FCSTD DOCUMENT  (FreeCAD 0.19R0.19.2)
Label: enclosure_000
License: All rights reserved
LicenseURL: http://en.wikipedia.org/wiki/All_rights_reserved
objects: Sketcher::SketchObject×1
note: 1 computed .brp shape members not serialized (recipe doc carries the construction recipe); baked Part::Feature solids carry a one-line shape summary decoded from their .brp

FEATURE [Sketcher::SketchObject] Sketch
  FullyConstrained = true
  sketch-geometry (13):
    g0: LineSegment StartX=0 StartY=0 StartZ=0 EndX=98 EndY=0 EndZ=0
    g1: LineSegment StartX=117 StartY=19 StartZ=0 EndX=117 EndY=38 EndZ=0
    g2: ArcOfCircle CenterX=98 CenterY=19 CenterZ=0 NormalX=0 NormalY=0 NormalZ=1 AngleXU=0 Radius=19 StartAngle=4.71239 EndAngle=6.28319
    g3: LineSegment StartX=0 StartY=0 StartZ=0 EndX=0 EndY=19 EndZ=0
    g4: LineSegment StartX=19 StartY=38 StartZ=0 EndX=117 EndY=38 EndZ=0
    g5: ArcOfCircle CenterX=19 CenterY=19 CenterZ=0 NormalX=0 NormalY=0 NormalZ=1 AngleXU=0 Radius=19 StartAngle=1.5708 EndAngle=3.14159
    g6: ArcOfCircle CenterX=19 CenterY=19 CenterZ=0 NormalX=0 NormalY=0 NormalZ=1 AngleXU=0 Radius=16 StartAngle=1.5708 EndAngle=3.14159
    g7: ArcOfCircle CenterX=98 CenterY=19 CenterZ=0 NormalX=0 NormalY=0 NormalZ=1 AngleXU=0 Radius=16 StartAngle=4.71239 EndAngle=6.28319
    g8: LineSegment StartX=114 StartY=19 StartZ=0 EndX=114 EndY=35 EndZ=0
    g9: LineSegment StartX=19 StartY=35 StartZ=0 EndX=114 EndY=35 EndZ=0
    g10: LineSegment StartX=117.858 StartY=9.01251 StartZ=0 EndX=104.12 EndY=9.01251 EndZ=0
    g11: LineSegment StartX=98 StartY=3 StartZ=0 EndX=-1.41284 EndY=3 EndZ=0
    g12: LineSegment StartX=3 StartY=19 StartZ=0 EndX=3 EndY=2.50571 EndZ=0
  constraints (36):
    c: Coincident(g0,g-1)
    c: Distance(g0) = 98
    c: Horizontal(g0)
    c: Vertical(g1)
    c: Distance(g1) = 19
    c: Block(g1)
    c: Coincident(g2,g0)
    c: Coincident(g2,g1)
    c: Block(g2)
    c: Vertical(g3)
    c: Equal(g1,g3) = 19
    c: Block(g3)
    c: Coincident(g3,g0)
    c: Coincident(g4,g1)
    c: Horizontal(g4)
    c: Distance(g4) = 98
    c: Coincident(g5,g4)
    c: Coincident(g5,g3)
    c: Block(g5)
    c: Coincident(g6,g5)
    c: Coincident(g7,g2)
    c: Block(g7)
    c: Block(g6)
    c: Coincident(g8,g7)
    c: Vertical(g8)
    c: Coincident(g9,g6)
    c: Horizontal(g9)
    c: Coincident(g8,g9)
    c: Horizontal(g10)
    c: Block(g10)
    c: Coincident(g11,g7)
    c: Horizontal(g11)
    c: Coincident(g12,g6)
    c: Vertical(g12)
    c: Block(g11)
    c: Block(g12)
